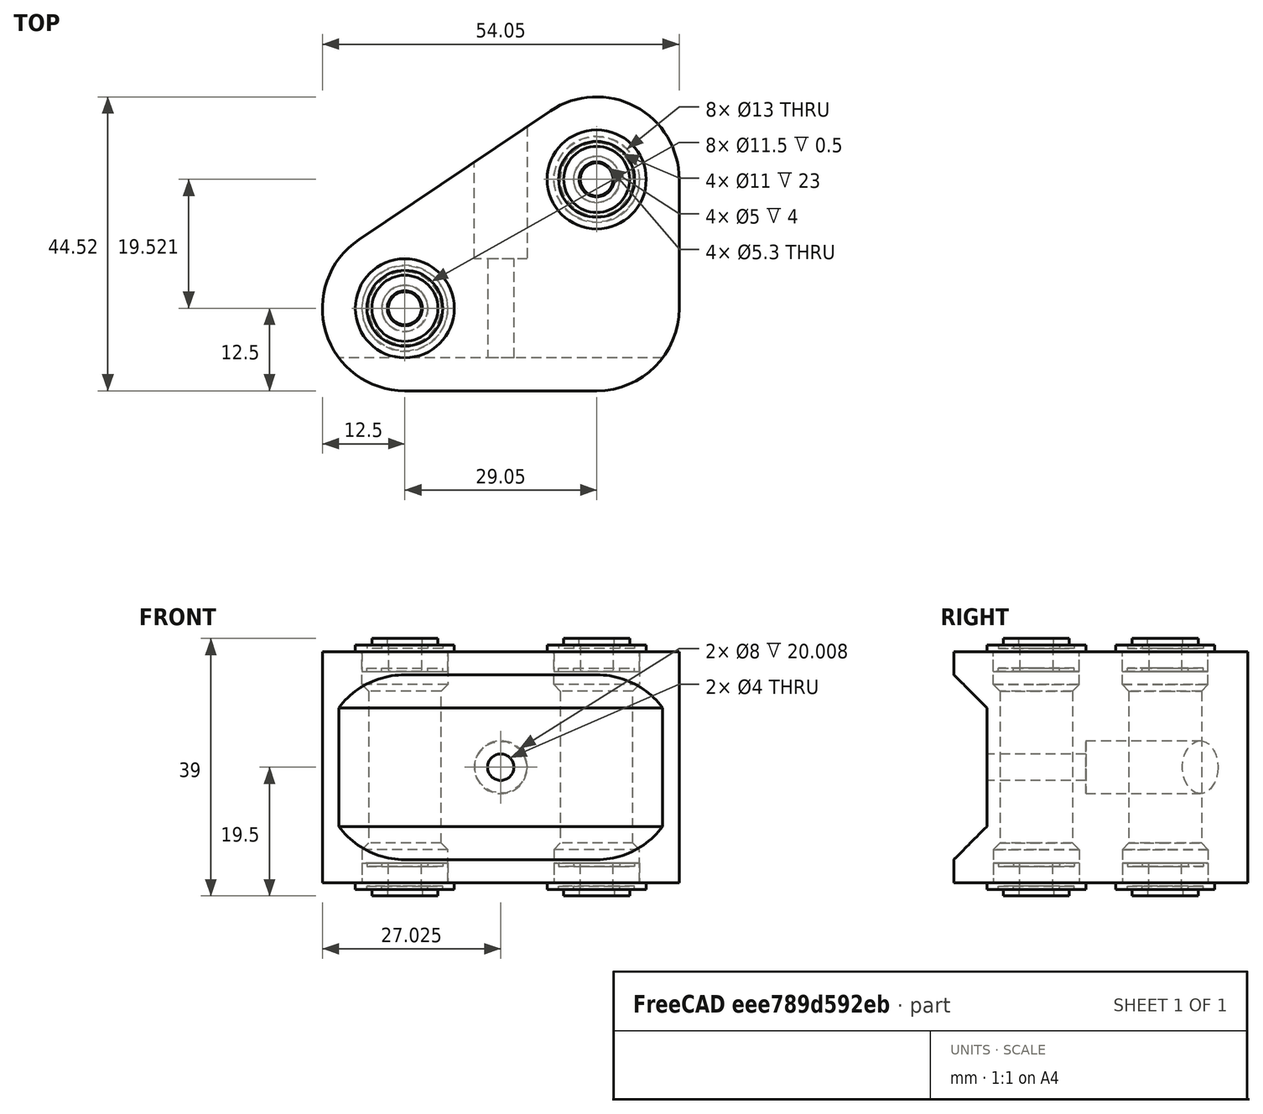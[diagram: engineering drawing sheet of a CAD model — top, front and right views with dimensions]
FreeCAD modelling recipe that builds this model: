
FCSTD DOCUMENT  (FreeCAD 0.20R29410 (Git))
Label: #0_ASSEMBLY_END_EFFECTOR
License: All rights reserved
LicenseURL: http://en.wikipedia.org/wiki/All_rights_reserved
objects: Part::FeaturePython×9, App::FeaturePython×8
note: 9 computed .brp shape members not serialized (recipe doc carries the construction recipe); baked Part::Feature solids carry a one-line shape summary decoded from their .brp

FEATURE [Part::FeaturePython] b__21_EndEffector_001_  label="#21_EndEffector_001"  # a2plus imported part (geometry in sourceFile) (typed FeaturePython)
  a2p_Version = 0.4.60k
  fixedPosition = true
  objectType = a2pPart
  sourceFile = .\#21_EndEffector.FCStd
  subassemblyImport = false
  timeLastImport = 1.68901e+09
  updateColors = true
FEATURE [Part::FeaturePython] b_F6951_001_  label="F6951_001"  # a2plus imported part (geometry in sourceFile) (typed FeaturePython)
  Placement = pos=(1.71249e-08,-2.8281e-09,32) rot=(0,0,1;0rad)
  a2p_Version = 0.4.60k
  fixedPosition = false
  objectType = a2pPart
  sourceFile = .\..\Complements\F695.step
  subassemblyImport = false
  timeLastImport = 1.6885e+09
  updateColors = true
FEATURE [Part::FeaturePython] b_F6951_001_001  label="F6951_002"  # a2plus imported part (geometry in sourceFile) (typed FeaturePython)
  Placement = pos=(-5.10256e-08,1.16971e-07,3) rot=(0.916552,0.399916,0;3.14159rad)
  a2p_Version = 0.4.60k
  fixedPosition = false
  objectType = a2pPart
  sourceFile = .\..\Complements\F695.step
  subassemblyImport = false
  timeLastImport = 1.6885e+09
  updateColors = true
FEATURE [Part::FeaturePython] b_F6951_001_002  label="F6951_003"  # a2plus imported part (geometry in sourceFile) (typed FeaturePython)
  Placement = pos=(29.0504,19.5211,3) rot=(0.884635,0.466284,0;3.14159rad)
  a2p_Version = 0.4.60k
  fixedPosition = false
  objectType = a2pPart
  sourceFile = .\..\Complements\F695.step
  subassemblyImport = false
  timeLastImport = 1.6885e+09
  updateColors = true
FEATURE [Part::FeaturePython] b_F6951_001_003  label="F6951_004"  # a2plus imported part (geometry in sourceFile) (typed FeaturePython)
  Placement = pos=(29.0504,19.5211,32) rot=(0,0,1;0rad)
  a2p_Version = 0.4.60k
  fixedPosition = false
  objectType = a2pPart
  sourceFile = .\..\Complements\F695.step
  subassemblyImport = false
  timeLastImport = 1.6885e+09
  updateColors = true
FEATURE [App::FeaturePython] circularEdge_001  label="circularEdge_001__#21_EndEffector_001"  # a2plus constraint (typed FeaturePython)
  Object1 = b_F6951_001_003
  Object2 = b__21_EndEffector_001_
  ParentTreeObject = -> b_F6951_001_003
  SubElement1 = Edge19
  SubElement2 = Edge41
  Suppressed = false
  Type = circularEdge
  directionConstraint = 0
  lockRotation = false
  offset = 0
FEATURE [App::FeaturePython] circularEdge_001_mirror  label="circularEdge_001__F6951_004"  # a2plus constraint (typed FeaturePython)
  Object1 = b_F6951_001_003
  Object2 = b__21_EndEffector_001_
  ParentTreeObject = -> b__21_EndEffector_001_
  SubElement1 = Edge19
  SubElement2 = Edge41
  Suppressed = false
  Type = circularEdge
  directionConstraint = 0
  lockRotation = false
  offset = 0
FEATURE [App::FeaturePython] circularEdge_002  label="circularEdge_002__#21_EndEffector_001"  # a2plus constraint (typed FeaturePython)
  Object1 = b_F6951_001_
  Object2 = b__21_EndEffector_001_
  ParentTreeObject = -> b_F6951_001_
  SubElement1 = Edge18
  SubElement2 = Edge40
  Suppressed = false
  Type = circularEdge
  directionConstraint = 0
  lockRotation = false
  offset = 0
FEATURE [App::FeaturePython] circularEdge_002_mirror  label="circularEdge_002__F6951_001"  # a2plus constraint (typed FeaturePython)
  Object1 = b_F6951_001_
  Object2 = b__21_EndEffector_001_
  ParentTreeObject = -> b__21_EndEffector_001_
  SubElement1 = Edge18
  SubElement2 = Edge40
  Suppressed = false
  Type = circularEdge
  directionConstraint = 0
  lockRotation = false
  offset = 0
FEATURE [App::FeaturePython] circularEdge_003  label="circularEdge_003__#21_EndEffector_001"  # a2plus constraint (typed FeaturePython)
  Object1 = b_F6951_001_002
  Object2 = b__21_EndEffector_001_
  ParentTreeObject = -> b_F6951_001_002
  SubElement1 = Edge19
  SubElement2 = Edge12
  Suppressed = false
  Type = circularEdge
  directionConstraint = 0
  lockRotation = false
  offset = 0
FEATURE [App::FeaturePython] circularEdge_003_mirror  label="circularEdge_003__F6951_003"  # a2plus constraint (typed FeaturePython)
  Object1 = b_F6951_001_002
  Object2 = b__21_EndEffector_001_
  ParentTreeObject = -> b__21_EndEffector_001_
  SubElement1 = Edge19
  SubElement2 = Edge12
  Suppressed = false
  Type = circularEdge
  directionConstraint = 0
  lockRotation = false
  offset = 0
FEATURE [App::FeaturePython] circularEdge_004  label="circularEdge_004__#21_EndEffector_001"  # a2plus constraint (typed FeaturePython)
  Object1 = b_F6951_001_001
  Object2 = b__21_EndEffector_001_
  ParentTreeObject = -> b_F6951_001_001
  SubElement1 = Edge19
  SubElement2 = Edge3
  Suppressed = false
  Type = circularEdge
  directionConstraint = 0
  lockRotation = false
  offset = 0
FEATURE [App::FeaturePython] circularEdge_004_mirror  label="circularEdge_004__F6951_002"  # a2plus constraint (typed FeaturePython)
  Object1 = b_F6951_001_001
  Object2 = b__21_EndEffector_001_
  ParentTreeObject = -> b__21_EndEffector_001_
  SubElement1 = Edge19
  SubElement2 = Edge3
  Suppressed = false
  Type = circularEdge
  directionConstraint = 0
  lockRotation = false
  offset = 0
FEATURE [Part::FeaturePython] Washer  label="M5-Arandela"  # Fasteners workbench fastener (typed FeaturePython)
  Placement = pos=(29.0504,19.5211,-1) rot=(0.884547,0.466452,0;3.14159rad)
  baseObject = -> b_F6951_001_002 [Edge17]
  diameter = 6
  invert = true
  matchOuter = false
  offset = 0
  type = 4
FEATURE [Part::FeaturePython] Washer001  label="M5-Arandela004"  # Fasteners workbench fastener (typed FeaturePython)
  Placement = pos=(3.96734e-08,-9.0947e-08,-1) rot=(0.916586,0.399838,0;3.14159rad)
  baseObject = -> b_F6951_001_001 [Edge17]
  diameter = 6
  invert = true
  matchOuter = false
  offset = 0
  type = 4
FEATURE [Part::FeaturePython] Washer002  label="M5-Arandela005"  # Fasteners workbench fastener (typed FeaturePython)
  Placement = pos=(29.0504,19.5211,36) rot=(0,0,1;0rad)
  baseObject = -> b_F6951_001_003 [Edge17]
  diameter = 6
  invert = true
  matchOuter = false
  offset = 0
  type = 4
FEATURE [Part::FeaturePython] Washer003  label="M5-Arandela006"  # Fasteners workbench fastener (typed FeaturePython)
  Placement = pos=(1.71249e-08,-2.8281e-09,36) rot=(0,0,1;0rad)
  baseObject = -> b_F6951_001_ [Edge17]
  diameter = 6
  invert = true
  matchOuter = false
  offset = 0
  type = 4
